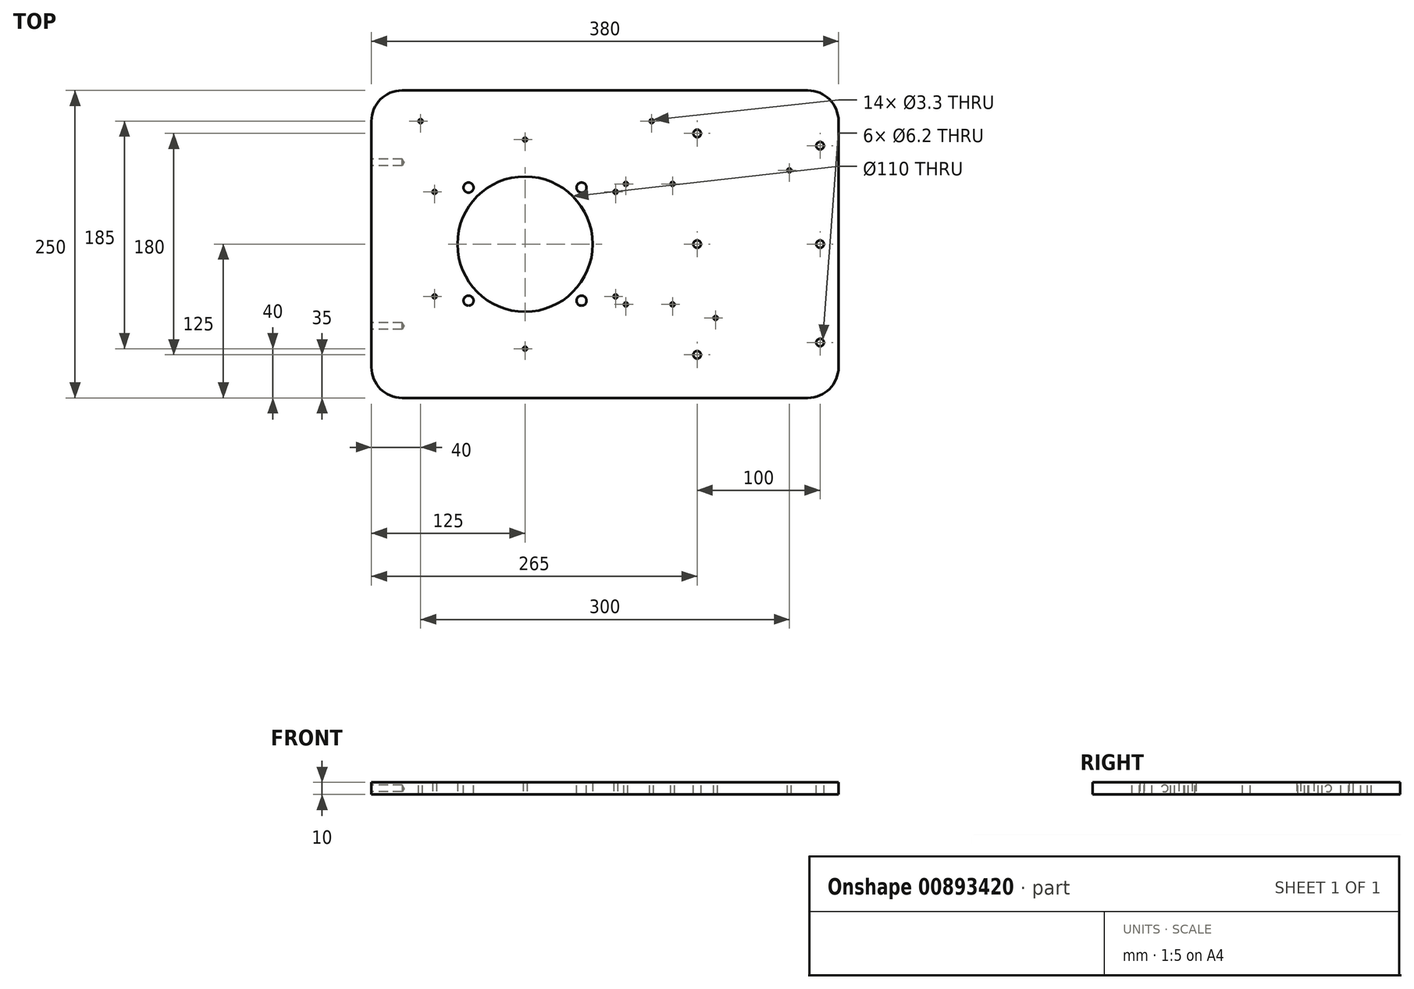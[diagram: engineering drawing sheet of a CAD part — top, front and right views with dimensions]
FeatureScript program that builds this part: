
annotation { "Feature Type Name" : "Feature", "Feature Type Description" : "" }
export const myFeature = defineFeature(function(context is Context, id is Id, definition is map)
    precondition{}
    {
        {
            var Q0;
            Q0=qCreatedBy(makeId("Top.planeOp"),FACE);
            var sketch = newSketch(context, id + "F0", { "sketchPlane" : qUnion([Q0])});
            skLineSegment(sketch, "E0.bottom", {"start": v(-100, -125) * mm, "end": v(-26.56, -125) * mm});
            skLineSegment(sketch, "E0.top", {"start": v(-100, 125) * mm, "end": v(-26.56, 125) * mm});
            skLineSegment(sketch, "E0.left", {"start": v(-125, -100) * mm, "end": v(-125, 100) * mm});
            skLineSegment(sketch, "E0.right", {"start": v(255, -100) * mm, "end": v(255, 100) * mm});
            skLineSegment(sketch, "E1.trimOffspring", {"start": v(118.7, 125) * mm, "end": v(230, 125) * mm});
            skLineSegment(sketch, "E2.trimOffspring", {"start": v(100.35, -125) * mm, "end": v(230, -125) * mm});
            skPoint(sketch, "E3.visualSharp", {"position": v(-125, 125) * mm});
            skArc(sketch, "E3.filletArc", {"start": v(-100, 125) * mm, "mid": v(-117.68, 117.68) * mm, "end": v(-125, 100) * mm});
            skPoint(sketch, "E4.visualSharp", {"position": v(-125, -125) * mm});
            skArc(sketch, "E4.filletArc", {"start": v(-125, -100) * mm, "mid": v(-117.68, -117.68) * mm, "end": v(-100, -125) * mm});
            skPoint(sketch, "E5.visualSharp", {"position": v(255, -125) * mm});
            skArc(sketch, "E5.filletArc", {"start": v(230, -125) * mm, "mid": v(247.68, -117.68) * mm, "end": v(255, -100) * mm});
            skPoint(sketch, "E6.visualSharp", {"position": v(255, 125) * mm});
            skArc(sketch, "E6.filletArc", {"start": v(255, 100) * mm, "mid": v(247.68, 117.68) * mm, "end": v(230, 125) * mm});
            skLineSegment(sketch, "E7.trimOffspring", {"start": v(-26.56, 125) * mm, "end": v(118.7, 125) * mm});
            skLineSegment(sketch, "E8.trimOffspring", {"start": v(-26.56, -125) * mm, "end": v(100.35, -125) * mm});
            skPoint(sketch, "E9.end.orphan", {"position": v(255, 0) * mm});
            skPoint(sketch, "E9.start.orphan", {"position": v(-125, 0) * mm});
            skCircle(sketch, "E10", {"center": v(0, 0) * mm, "radius": 55 * mm});
            skSolve(sketch);
        }
        {
            var Q0;
            Q0=makeQuery(id+"F0.imprint","IMPRINT",FACE,{"disambiguationData":[TD([[makeQuery(id+"F0.imprint","IMPRINT",EDGE,{"derivedFrom":sQuery(id+"F0.wireOp",EDGE,"E0.bottom")}),1.0]])]});
            extrude(context, id + "F1", {"entities" : qUnion([Q0]), "depth" : 10 * mm, "offsetDistance" : 25 * mm});
        }
        {
            var Q0;
            Q0=makeQuery(id+"F1.opExtrude","CAP_FACE",FACE,{"disambiguationData":[OSD([sQuery(id+"F0.wireOp",EDGE,"E0.bottom"),sQuery(id+"F0.wireOp",EDGE,"E0.top"),sQuery(id+"F0.wireOp",EDGE,"E0.left"),sQuery(id+"F0.wireOp",EDGE,"E0.right"),sQuery(id+"F0.wireOp",EDGE,"E1.trimOffspring"),sQuery(id+"F0.wireOp",EDGE,"E2.trimOffspring"),sQuery(id+"F0.wireOp",EDGE,"E3.filletArc"),sQuery(id+"F0.wireOp",EDGE,"E4.filletArc"),sQuery(id+"F0.wireOp",EDGE,"E5.filletArc"),sQuery(id+"F0.wireOp",EDGE,"E6.filletArc"),sQuery(id+"F0.wireOp",EDGE,"E7.trimOffspring"),sQuery(id+"F0.wireOp",EDGE,"E8.trimOffspring"),sQuery(id+"F0.wireOp",EDGE,"E10")])],"isStart":false});
            var sketch = newSketch(context, id + "F2", { "sketchPlane" : qUnion([Q0])});
            skCircle(sketch, "E11", {"center": v(45.96, 45.96) * mm, "radius": 4.1 * mm});
            skCircle(sketch, "E12.1.0", {"center": v(-45.96, 45.96) * mm, "radius": 4.1 * mm});
            skCircle(sketch, "E12.2.0", {"center": v(-45.96, -45.96) * mm, "radius": 4.1 * mm});
            skCircle(sketch, "E12.3.0", {"center": v(45.96, -45.96) * mm, "radius": 4.1 * mm});
            skPoint(sketch, "E12.center", {"position": v(0, 0) * mm});
            skSolve(sketch);
        }
        {
            var Q0;
            Q0=makeQuery(id+"F2.imprint","IMPRINT",FACE,{"disambiguationData":[TD([[makeQuery(id+"F2.imprint","IMPRINT",EDGE,{"derivedFrom":sQuery(id+"F2.wireOp",EDGE,"E12.1.0")}),1.0]])]});
            var Q1;
            Q1=makeQuery(id+"F2.imprint","IMPRINT",FACE,{"disambiguationData":[TD([[makeQuery(id+"F2.imprint","IMPRINT",EDGE,{"derivedFrom":sQuery(id+"F2.wireOp",EDGE,"E11")}),1.0]])]});
            var Q2;
            Q2=makeQuery(id+"F2.imprint","IMPRINT",FACE,{"disambiguationData":[TD([[makeQuery(id+"F2.imprint","IMPRINT",EDGE,{"derivedFrom":sQuery(id+"F2.wireOp",EDGE,"E12.3.0")}),1.0]])]});
            var Q3;
            Q3=makeQuery(id+"F2.imprint","IMPRINT",FACE,{"disambiguationData":[TD([[makeQuery(id+"F2.imprint","IMPRINT",EDGE,{"derivedFrom":sQuery(id+"F2.wireOp",EDGE,"E12.2.0")}),1.0]])]});
            extrude(context, id + "F3", {"entities" : qUnion([Q0, Q1, Q2, Q3]), "operationType" : NewBodyOperationType.REMOVE, "oppositeDirection" : true, "depth" : 25 * mm, "offsetDistance" : 25 * mm});
        }
        {
            var Q0;
            Q0=makeQuery(id+"F1.opExtrude","CAP_FACE",FACE,{"disambiguationData":[OSD([sQuery(id+"F0.wireOp",EDGE,"E0.bottom"),sQuery(id+"F0.wireOp",EDGE,"E0.top"),sQuery(id+"F0.wireOp",EDGE,"E0.left"),sQuery(id+"F0.wireOp",EDGE,"E0.right"),sQuery(id+"F0.wireOp",EDGE,"E1.trimOffspring"),sQuery(id+"F0.wireOp",EDGE,"E2.trimOffspring"),sQuery(id+"F0.wireOp",EDGE,"E3.filletArc"),sQuery(id+"F0.wireOp",EDGE,"E4.filletArc"),sQuery(id+"F0.wireOp",EDGE,"E5.filletArc"),sQuery(id+"F0.wireOp",EDGE,"E6.filletArc"),sQuery(id+"F0.wireOp",EDGE,"E7.trimOffspring"),sQuery(id+"F0.wireOp",EDGE,"E8.trimOffspring"),sQuery(id+"F0.wireOp",EDGE,"E10")])],"isStart":false});
            var sketch = newSketch(context, id + "F4", { "sketchPlane" : qUnion([Q0])});
            skCircle(sketch, "E13", {"center": v(240, 80) * mm, "radius": 3.1 * mm});
            skCircle(sketch, "E14", {"center": v(140, 90) * mm, "radius": 3.1 * mm});
            skCircle(sketch, "E15", {"center": v(140, 0) * mm, "radius": 3.1 * mm});
            skCircle(sketch, "E16", {"center": v(240, 0) * mm, "radius": 3.1 * mm});
            skCircle(sketch, "E17", {"center": v(140, -90) * mm, "radius": 3.1 * mm});
            skCircle(sketch, "E18", {"center": v(240, -80) * mm, "radius": 3.1 * mm});
            skSolve(sketch);
        }
        {
            var Q0;
            Q0=makeQuery(id+"F4.imprint","IMPRINT",FACE,{"disambiguationData":[TD([[makeQuery(id+"F4.imprint","IMPRINT",EDGE,{"derivedFrom":sQuery(id+"F4.wireOp",EDGE,"E14")}),1.0]])]});
            var Q1;
            Q1=makeQuery(id+"F4.imprint","IMPRINT",FACE,{"disambiguationData":[TD([[makeQuery(id+"F4.imprint","IMPRINT",EDGE,{"derivedFrom":sQuery(id+"F4.wireOp",EDGE,"E15")}),1.0]])]});
            var Q2;
            Q2=makeQuery(id+"F4.imprint","IMPRINT",FACE,{"disambiguationData":[TD([[makeQuery(id+"F4.imprint","IMPRINT",EDGE,{"derivedFrom":sQuery(id+"F4.wireOp",EDGE,"E17")}),1.0]])]});
            var Q3;
            Q3=makeQuery(id+"F4.imprint","IMPRINT",FACE,{"disambiguationData":[TD([[makeQuery(id+"F4.imprint","IMPRINT",EDGE,{"derivedFrom":sQuery(id+"F4.wireOp",EDGE,"E18")}),1.0]])]});
            var Q4;
            Q4=makeQuery(id+"F4.imprint","IMPRINT",FACE,{"disambiguationData":[TD([[makeQuery(id+"F4.imprint","IMPRINT",EDGE,{"derivedFrom":sQuery(id+"F4.wireOp",EDGE,"E16")}),1.0]])]});
            var Q5;
            Q5=makeQuery(id+"F4.imprint","IMPRINT",FACE,{"disambiguationData":[TD([[makeQuery(id+"F4.imprint","IMPRINT",EDGE,{"derivedFrom":sQuery(id+"F4.wireOp",EDGE,"E13")}),1.0]])]});
            extrude(context, id + "F5", {"entities" : qUnion([Q0, Q1, Q2, Q3, Q4, Q5]), "operationType" : NewBodyOperationType.REMOVE, "oppositeDirection" : true, "depth" : 25 * mm, "offsetDistance" : 25 * mm});
        }
        {
            var Q0;
            Q0=makeQuery(id+"F1.opExtrude","SWEPT_FACE",FACE,{"disambiguationData":[OSD([sQuery(id+"F0.wireOp",EDGE,"E0.left")])]});
            var sketch = newSketch(context, id + "F6", { "sketchPlane" : qUnion([Q0])});
            skPoint(sketch, "E19", {"position": v(-66.5, 5) * mm});
            skPoint(sketch, "E20", {"position": v(66.5, 5) * mm});
            skSolve(sketch);
        }
        {
            var Q0;
            Q0=sQuery(id+"F6.wireOp",VERTEX,"E19");
            var Q1;
            Q1=sQuery(id+"F6.wireOp",VERTEX,"E20");
            var Q2;
            Q2=makeQuery(id+"F1.opExtrude","SWEPT_BODY",BODY,{"disambiguationData":[OSD([sQuery(id+"F0.wireOp",EDGE,"E0.bottom"),sQuery(id+"F0.wireOp",EDGE,"E0.top"),sQuery(id+"F0.wireOp",EDGE,"E0.left"),sQuery(id+"F0.wireOp",EDGE,"E0.right"),sQuery(id+"F0.wireOp",EDGE,"E1.trimOffspring"),sQuery(id+"F0.wireOp",EDGE,"E2.trimOffspring"),sQuery(id+"F0.wireOp",EDGE,"E3.filletArc"),sQuery(id+"F0.wireOp",EDGE,"E4.filletArc"),sQuery(id+"F0.wireOp",EDGE,"E5.filletArc"),sQuery(id+"F0.wireOp",EDGE,"E6.filletArc"),sQuery(id+"F0.wireOp",EDGE,"E7.trimOffspring"),sQuery(id+"F0.wireOp",EDGE,"E8.trimOffspring"),sQuery(id+"F0.wireOp",EDGE,"E10")])]});
            hole(context, id + "F7", {"style" : HoleStyle.SIMPLE, "endStyle" : HoleEndStyle.BLIND, "standardTappedOrClearance" : lookupTablePath({ "fit" : "Normal", "standard" : "ISO", "size" : "M5", "type" : "Clearance" }), "standardBlindInLast" : lookupTablePath({ "fit" : "Normal", "standard" : "ISO", "engagement" : "75%", "pitch" : "0.8 mm", "size" : "M5", "type" : "Clearance & tapped" }), "holeDiameter" : 5.5 * mm, "majorDiameter" : 5 * mm, "holeDepth" : 25 * mm, "isTappedThrough" : true, "tappedDepth" : 12 * mm, "tapClearance" : 3, "locations" : qUnion([Q0, Q1]), "scope" : qUnion([Q2])});
        }
        {
            var Q0;
            Q0=makeQuery(id+"F4.imprint","IMPRINT",FACE,{"disambiguationData":[TD([[makeQuery(id+"F4.imprint","IMPRINT",EDGE,{"derivedFrom":sQuery(id+"F4.wireOp",EDGE,"E13")}),-1.0]])]});
            var sketch = newSketch(context, id + "F8", { "sketchPlane" : qUnion([Q0])});
            skPoint(sketch, "E21", {"position": v(82, 49) * mm});
            skPoint(sketch, "E22", {"position": v(120, 49) * mm});
            skPoint(sketch, "E23", {"position": v(82, -49) * mm});
            skPoint(sketch, "E24", {"position": v(120, -49) * mm});
            skSolve(sketch);
        }
        {
            var Q0;
            Q0=sQuery(id+"F8.wireOp",VERTEX,"E21");
            var Q1;
            Q1=sQuery(id+"F8.wireOp",VERTEX,"E22");
            var Q2;
            Q2=sQuery(id+"F8.wireOp",VERTEX,"E24");
            var Q3;
            Q3=sQuery(id+"F8.wireOp",VERTEX,"E23");
            var Q4;
            Q4=makeQuery(id+"F1.opExtrude","SWEPT_BODY",BODY,{"disambiguationData":[OSD([sQuery(id+"F0.wireOp",EDGE,"E0.bottom"),sQuery(id+"F0.wireOp",EDGE,"E0.top"),sQuery(id+"F0.wireOp",EDGE,"E0.left"),sQuery(id+"F0.wireOp",EDGE,"E0.right"),sQuery(id+"F0.wireOp",EDGE,"E1.trimOffspring"),sQuery(id+"F0.wireOp",EDGE,"E2.trimOffspring"),sQuery(id+"F0.wireOp",EDGE,"E3.filletArc"),sQuery(id+"F0.wireOp",EDGE,"E4.filletArc"),sQuery(id+"F0.wireOp",EDGE,"E5.filletArc"),sQuery(id+"F0.wireOp",EDGE,"E6.filletArc"),sQuery(id+"F0.wireOp",EDGE,"E7.trimOffspring"),sQuery(id+"F0.wireOp",EDGE,"E8.trimOffspring"),sQuery(id+"F0.wireOp",EDGE,"E10")])]});
            hole(context, id + "F9", {"style" : HoleStyle.SIMPLE, "endStyle" : HoleEndStyle.BLIND, "standardTappedOrClearance" : lookupTablePath({ "standard" : "ISO", "engagement" : "75%", "pitch" : "0.7 mm", "size" : "M4", "type" : "Tapped" }), "standardBlindInLast" : lookupTablePath({ "standard" : "ISO", "fit" : "Normal", "engagement" : "75%", "pitch" : "0.7 mm", "size" : "M4", "type" : "Clearance & tapped" }), "holeDiameter" : 3.3 * mm, "majorDiameter" : 4 * mm, "showTappedDepth" : true, "holeDepth" : 14.1 * mm, "isTappedThrough" : true, "tappedDepth" : 12 * mm, "tapClearance" : 3, "startFromSketch" : true, "locations" : qUnion([Q0, Q1, Q2, Q3]), "scope" : qUnion([Q4])});
        }
        {
            var Q0;
            Q0=makeQuery(id+"F4.imprint","IMPRINT",FACE,{"disambiguationData":[TD([[makeQuery(id+"F4.imprint","IMPRINT",EDGE,{"derivedFrom":sQuery(id+"F4.wireOp",EDGE,"E13")}),-1.0]])]});
            var sketch = newSketch(context, id + "F10", { "sketchPlane" : qUnion([Q0])});
            skPoint(sketch, "E25", {"position": v(-85, 100) * mm});
            skPoint(sketch, "E26", {"position": v(103, 100) * mm});
            skSolve(sketch);
        }
        {
            var Q0;
            Q0=sQuery(id+"F10.wireOp",VERTEX,"E25");
            var Q1;
            Q1=sQuery(id+"F10.wireOp",VERTEX,"E26");
            var Q2;
            Q2=makeQuery(id+"F1.opExtrude","SWEPT_BODY",BODY,{"disambiguationData":[OSD([sQuery(id+"F0.wireOp",EDGE,"E0.bottom"),sQuery(id+"F0.wireOp",EDGE,"E0.top"),sQuery(id+"F0.wireOp",EDGE,"E0.left"),sQuery(id+"F0.wireOp",EDGE,"E0.right"),sQuery(id+"F0.wireOp",EDGE,"E1.trimOffspring"),sQuery(id+"F0.wireOp",EDGE,"E2.trimOffspring"),sQuery(id+"F0.wireOp",EDGE,"E3.filletArc"),sQuery(id+"F0.wireOp",EDGE,"E4.filletArc"),sQuery(id+"F0.wireOp",EDGE,"E5.filletArc"),sQuery(id+"F0.wireOp",EDGE,"E6.filletArc"),sQuery(id+"F0.wireOp",EDGE,"E7.trimOffspring"),sQuery(id+"F0.wireOp",EDGE,"E8.trimOffspring"),sQuery(id+"F0.wireOp",EDGE,"E10")])]});
            hole(context, id + "F11", {"style" : HoleStyle.SIMPLE, "endStyle" : HoleEndStyle.BLIND, "standardTappedOrClearance" : lookupTablePath({ "standard" : "ISO", "engagement" : "75%", "pitch" : "0.7 mm", "size" : "M4", "type" : "Tapped" }), "standardBlindInLast" : lookupTablePath({ "standard" : "ISO", "fit" : "Normal", "engagement" : "75%", "pitch" : "0.7 mm", "size" : "M4", "type" : "Clearance & tapped" }), "holeDiameter" : 3.3 * mm, "majorDiameter" : 4 * mm, "showTappedDepth" : true, "holeDepth" : 14.1 * mm, "isTappedThrough" : true, "tappedDepth" : 12 * mm, "tapClearance" : 3, "locations" : qUnion([Q0, Q1]), "scope" : qUnion([Q2])});
        }
        {
            var Q0;
            Q0=makeQuery(id+"F1.opExtrude","CAP_FACE",FACE,{"disambiguationData":[OSD([sQuery(id+"F0.wireOp",EDGE,"E0.bottom"),sQuery(id+"F0.wireOp",EDGE,"E0.top"),sQuery(id+"F0.wireOp",EDGE,"E0.left"),sQuery(id+"F0.wireOp",EDGE,"E0.right"),sQuery(id+"F0.wireOp",EDGE,"E1.trimOffspring"),sQuery(id+"F0.wireOp",EDGE,"E2.trimOffspring"),sQuery(id+"F0.wireOp",EDGE,"E3.filletArc"),sQuery(id+"F0.wireOp",EDGE,"E4.filletArc"),sQuery(id+"F0.wireOp",EDGE,"E5.filletArc"),sQuery(id+"F0.wireOp",EDGE,"E6.filletArc"),sQuery(id+"F0.wireOp",EDGE,"E7.trimOffspring"),sQuery(id+"F0.wireOp",EDGE,"E8.trimOffspring"),sQuery(id+"F0.wireOp",EDGE,"E10")])],"isStart":true});
            var sketch = newSketch(context, id + "F12", { "sketchPlane" : qUnion([Q0])});
            skCircle(sketch, "E27", {"center": v(0, 85) * mm, "radius": 2 * mm});
            skCircle(sketch, "E28.1.0", {"center": v(-73.61, 42.5) * mm, "radius": 2 * mm});
            skCircle(sketch, "E28.2.0", {"center": v(-73.61, -42.5) * mm, "radius": 2 * mm});
            skCircle(sketch, "E28.3.0", {"center": v(0, -85) * mm, "radius": 2 * mm});
            skCircle(sketch, "E28.4.0", {"center": v(73.61, -42.5) * mm, "radius": 2 * mm});
            skCircle(sketch, "E28.5.0", {"center": v(73.61, 42.5) * mm, "radius": 2 * mm});
            skPoint(sketch, "E28.center", {"position": v(0, 0) * mm});
            skSolve(sketch);
        }
        {
            var Q0;
            Q0=makeQuery(id+"F4.imprint","IMPRINT",FACE,{"disambiguationData":[TD([[makeQuery(id+"F4.imprint","IMPRINT",EDGE,{"derivedFrom":sQuery(id+"F4.wireOp",EDGE,"E13")}),-1.0]])]});
            var sketch = newSketch(context, id + "F13", { "sketchPlane" : qUnion([Q0])});
            skPoint(sketch, "E29", {"position": v(155, -60) * mm});
            skPoint(sketch, "E30", {"position": v(215, 60) * mm});
            skSolve(sketch);
        }
        {
            var Q0;
            Q0=sQuery(id+"F13.wireOp",VERTEX,"E30");
            var Q1;
            Q1=sQuery(id+"F13.wireOp",VERTEX,"E29");
            var Q2;
            Q2=makeQuery(id+"F1.opExtrude","SWEPT_BODY",BODY,{"disambiguationData":[OSD([sQuery(id+"F0.wireOp",EDGE,"E0.bottom"),sQuery(id+"F0.wireOp",EDGE,"E0.top"),sQuery(id+"F0.wireOp",EDGE,"E0.left"),sQuery(id+"F0.wireOp",EDGE,"E0.right"),sQuery(id+"F0.wireOp",EDGE,"E1.trimOffspring"),sQuery(id+"F0.wireOp",EDGE,"E2.trimOffspring"),sQuery(id+"F0.wireOp",EDGE,"E3.filletArc"),sQuery(id+"F0.wireOp",EDGE,"E4.filletArc"),sQuery(id+"F0.wireOp",EDGE,"E5.filletArc"),sQuery(id+"F0.wireOp",EDGE,"E6.filletArc"),sQuery(id+"F0.wireOp",EDGE,"E7.trimOffspring"),sQuery(id+"F0.wireOp",EDGE,"E8.trimOffspring"),sQuery(id+"F0.wireOp",EDGE,"E10")])]});
            hole(context, id + "F14", {"style" : HoleStyle.SIMPLE, "endStyle" : HoleEndStyle.BLIND, "standardTappedOrClearance" : lookupTablePath({ "standard" : "ISO", "engagement" : "75%", "pitch" : "0.7 mm", "size" : "M4", "type" : "Tapped" }), "standardBlindInLast" : lookupTablePath({ "fit" : "Normal", "standard" : "ISO", "engagement" : "75%", "pitch" : "0.7 mm", "size" : "M4", "type" : "Clearance & tapped" }), "holeDiameter" : 3.3 * mm, "majorDiameter" : 4 * mm, "showTappedDepth" : true, "holeDepth" : 14.1 * mm, "isTappedThrough" : true, "tappedDepth" : 12 * mm, "tapClearance" : 3, "locations" : qUnion([Q0, Q1]), "scope" : qUnion([Q2])});
        }
        {
            var Q0;
            Q0=sQuery(id+"F12.wireOp",VERTEX,"E28.2.0.center");
            var Q1;
            Q1=sQuery(id+"F12.wireOp",VERTEX,"E28.1.0.center");
            var Q2;
            Q2=sQuery(id+"F12.wireOp",VERTEX,"E27.center");
            var Q3;
            Q3=sQuery(id+"F12.wireOp",VERTEX,"E28.5.0.center");
            var Q4;
            Q4=sQuery(id+"F12.wireOp",VERTEX,"E28.4.0.center");
            var Q5;
            Q5=sQuery(id+"F12.wireOp",VERTEX,"E28.3.0.center");
            var Q6;
            Q6=makeQuery(id+"F1.opExtrude","SWEPT_BODY",BODY,{"disambiguationData":[OSD([sQuery(id+"F0.wireOp",EDGE,"E0.bottom"),sQuery(id+"F0.wireOp",EDGE,"E0.top"),sQuery(id+"F0.wireOp",EDGE,"E0.left"),sQuery(id+"F0.wireOp",EDGE,"E0.right"),sQuery(id+"F0.wireOp",EDGE,"E1.trimOffspring"),sQuery(id+"F0.wireOp",EDGE,"E2.trimOffspring"),sQuery(id+"F0.wireOp",EDGE,"E3.filletArc"),sQuery(id+"F0.wireOp",EDGE,"E4.filletArc"),sQuery(id+"F0.wireOp",EDGE,"E5.filletArc"),sQuery(id+"F0.wireOp",EDGE,"E6.filletArc"),sQuery(id+"F0.wireOp",EDGE,"E7.trimOffspring"),sQuery(id+"F0.wireOp",EDGE,"E8.trimOffspring"),sQuery(id+"F0.wireOp",EDGE,"E10")])]});
            hole(context, id + "F15", {"style" : HoleStyle.SIMPLE, "endStyle" : HoleEndStyle.BLIND, "standardTappedOrClearance" : lookupTablePath({ "standard" : "ISO", "engagement" : "75%", "pitch" : "0.7 mm", "size" : "M4", "type" : "Tapped" }), "standardBlindInLast" : lookupTablePath({ "fit" : "Normal", "standard" : "ISO", "engagement" : "75%", "pitch" : "0.7 mm", "size" : "M4", "type" : "Clearance & tapped" }), "holeDiameter" : 3.3 * mm, "majorDiameter" : 4 * mm, "showTappedDepth" : true, "holeDepth" : 14.1 * mm, "isTappedThrough" : true, "tappedDepth" : 12 * mm, "tapClearance" : 3, "locations" : qUnion([Q0, Q1, Q2, Q3, Q4, Q5]), "scope" : qUnion([Q6])});
        }
    });
